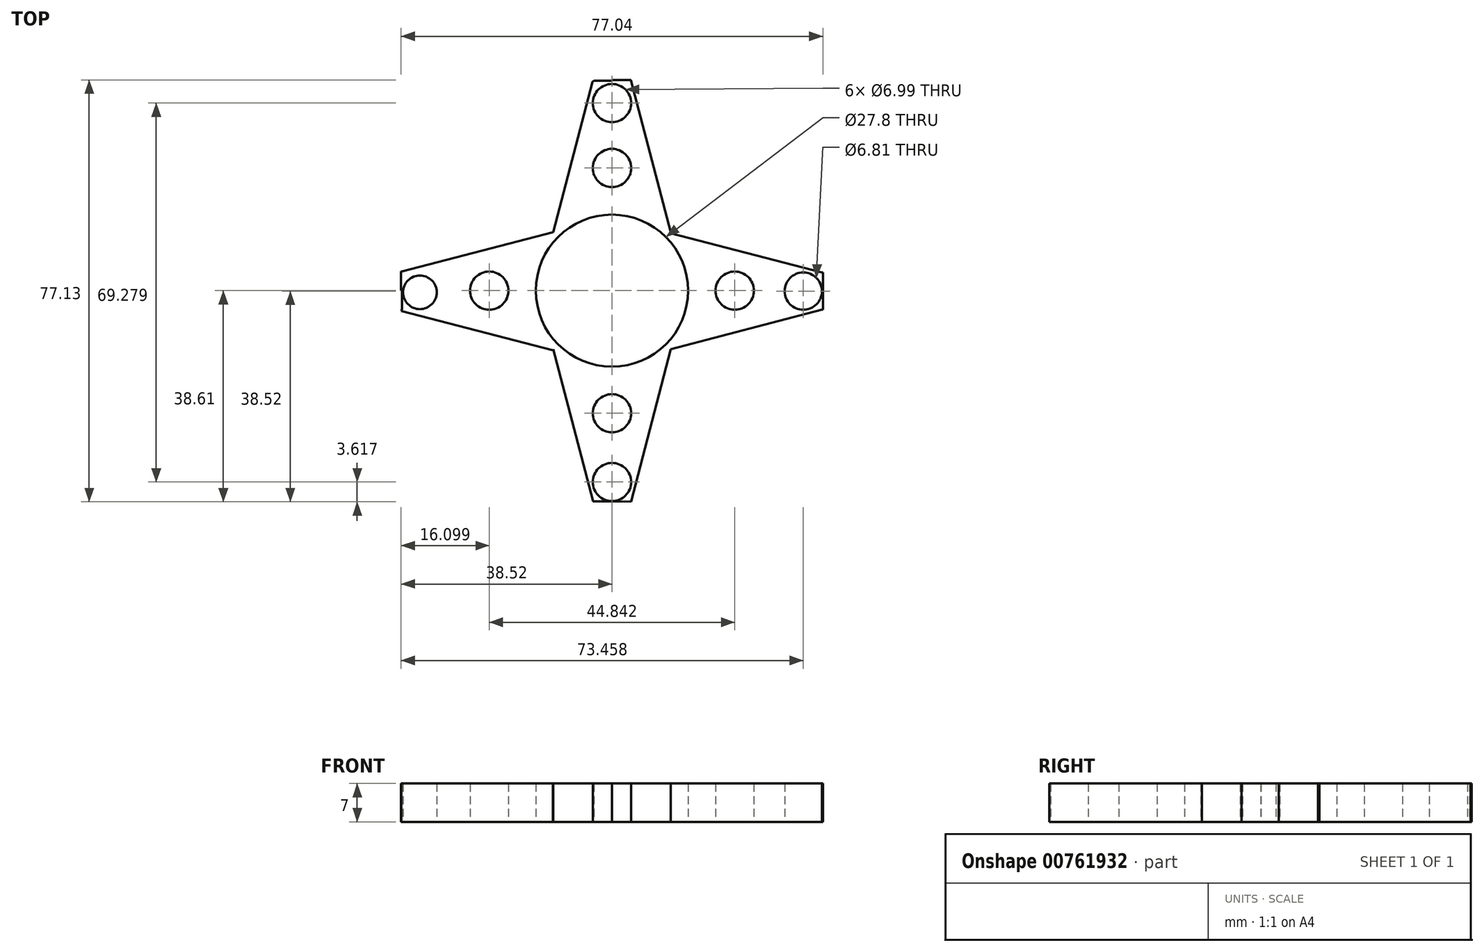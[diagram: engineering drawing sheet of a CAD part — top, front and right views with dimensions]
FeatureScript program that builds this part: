
annotation { "Feature Type Name" : "Feature", "Feature Type Description" : "" }
export const myFeature = defineFeature(function(context is Context, id is Id, definition is map)
    precondition{}
    {
        {
            var Q0;
            Q0=qCreatedBy(makeId("Top.planeOp"),FACE);
            var sketch = newSketch(context, id + "F0", { "sketchPlane" : qUnion([Q0])});
            skCircle(sketch, "E0", {"center": v(0, 0) * mm, "radius": 13.9 * mm});
            skPoint(sketch, "E1.start.orphan", {"position": v(7.44, 39.96) * mm});
            skPoint(sketch, "E2.start.orphan", {"position": v(0, 26.64) * mm});
            skPoint(sketch, "E3.orphan", {"position": v(0, 13.32) * mm});
            skPoint(sketch, "E4.MirrorCS.end.orphan", {"position": v(0, 39.96) * mm});
            skPoint(sketch, "E5.orphan", {"position": v(8.68, 13.32) * mm});
            skPoint(sketch, "E6.MirrorCS.end.orphan", {"position": v(-8.75, 13.32) * mm});
            skPoint(sketch, "E7.orphan", {"position": v(0, 30.02) * mm});
            skPoint(sketch, "E8.MirrorCS.start.orphan", {"position": v(0, 38.56) * mm});
            skCircle(sketch, "E9", {"center": v(0, 34.29) * mm, "radius": 3.5 * mm});
            skCircle(sketch, "E10.1.1", {"center": v(-35.09, -0.3) * mm, "radius": 3.08 * mm});
            skCircle(sketch, "E10.2.1", {"center": v(0, -35) * mm, "radius": 3.5 * mm});
            skCircle(sketch, "E10.3.1", {"center": v(34.94, -0.09) * mm, "radius": 3.4 * mm});
            skPoint(sketch, "E11.orphan", {"position": v(0, -13.9) * mm});
            skPoint(sketch, "E12.orphan", {"position": v(13.32, 0) * mm});
            skPoint(sketch, "E13.orphan", {"position": v(0, -13.32) * mm});
            skPoint(sketch, "E14.start.orphan", {"position": v(0, 13.9) * mm});
            skCircle(sketch, "E15.MirrorC", {"center": v(-22.42, 0) * mm, "radius": 3.5 * mm});
            skCircle(sketch, "E16.1.0", {"center": v(0, -22.42) * mm, "radius": 3.5 * mm});
            skCircle(sketch, "E16.2.0", {"center": v(22.42, 0) * mm, "radius": 3.5 * mm});
            skCircle(sketch, "E16.3.0", {"center": v(0, 22.42) * mm, "radius": 3.5 * mm});
            skPoint(sketch, "E17.orphan", {"position": v(-29.02, 12.82) * mm});
            skPoint(sketch, "E18.orphan", {"position": v(-13.9, 0) * mm});
            skPoint(sketch, "E19.orphan", {"position": v(-29.02, -0.23) * mm});
            skPoint(sketch, "E20.start.orphan", {"position": v(-22.96, -0.15) * mm});
            skPoint(sketch, "E21.start.orphan", {"position": v(-32.01, -0.3) * mm});
            skPoint(sketch, "E22.start.orphan", {"position": v(34.94, -3.5) * mm});
            skPoint(sketch, "E23.start.orphan", {"position": v(38.33, -3.5) * mm});
            skPoint(sketch, "E24.start.orphan", {"position": v(34.94, 3.32) * mm});
            skLineSegment(sketch, "E25.MirrorCS", {"start": v(38.52, 0) * mm, "end": v(38.52, -3.5) * mm});
            skLineSegment(sketch, "E26", {"start": v(38.35, 3.32) * mm, "end": v(10.66, 10.5) * mm});
            skLineSegment(sketch, "E27", {"start": v(38.33, -3.5) * mm, "end": v(10.71, -10.71) * mm});
            skPoint(sketch, "E28.start.orphan", {"position": v(3.5, 34.29) * mm});
            skPoint(sketch, "E29.start.orphan", {"position": v(-3.5, 34.29) * mm});
            skPoint(sketch, "E30.start.orphan", {"position": v(-35.09, 2.77) * mm});
            skPoint(sketch, "E31.start.orphan", {"position": v(-35.09, -3.38) * mm});
            skPoint(sketch, "E32.start.orphan", {"position": v(3.5, -35) * mm});
            skPoint(sketch, "E33.start.orphan", {"position": v(-3.5, -35) * mm});
            skPoint(sketch, "E34.orphan", {"position": v(-16.14, 34.94) * mm});
            skPoint(sketch, "E35.orphan", {"position": v(3.77, -14.48) * mm});
            skLineSegment(sketch, "E36.1.0", {"start": v(0.09, 38.35) * mm, "end": v(-3.32, 38.35) * mm});
            skLineSegment(sketch, "E36.1.1", {"start": v(3.5, 38.33) * mm, "end": v(10.71, 10.71) * mm});
            skLineSegment(sketch, "E36.1.2", {"start": v(0, 38.52) * mm, "end": v(3.5, 38.52) * mm});
            skLineSegment(sketch, "E36.2.0", {"start": v(-38.35, 0.09) * mm, "end": v(-38.35, -3.32) * mm});
            skLineSegment(sketch, "E36.2.1", {"start": v(-38.33, 3.5) * mm, "end": v(-10.71, 10.71) * mm});
            skLineSegment(sketch, "E36.2.2", {"start": v(-38.52, 0) * mm, "end": v(-38.52, 3.5) * mm});
            skLineSegment(sketch, "E36.3.0", {"start": v(-0.09, -38.35) * mm, "end": v(3.32, -38.35) * mm});
            skLineSegment(sketch, "E36.3.1", {"start": v(-3.5, -38.33) * mm, "end": v(-10.71, -10.71) * mm});
            skLineSegment(sketch, "E36.3.2", {"start": v(0, -38.52) * mm, "end": v(-3.5, -38.52) * mm});
            skLineSegment(sketch, "E37.1.0", {"start": v(-3.58, 38.2) * mm, "end": v(-10.77, 10.5) * mm});
            skLineSegment(sketch, "E37.2.0", {"start": v(-38.45, -3.74) * mm, "end": v(-10.77, -10.92) * mm});
            skLineSegment(sketch, "E37.3.0", {"start": v(3.47, -38.6) * mm, "end": v(10.66, -10.92) * mm});
            skPoint(sketch, "E37.center", {"position": v(-0.05, -0.2) * mm});
            skPoint(sketch, "E38.orphan", {"position": v(3.92, 14.64) * mm});
            skLineSegment(sketch, "E39", {"start": v(3.5, 38.52) * mm, "end": v(3.5, 38.33) * mm});
            skLineSegment(sketch, "E40", {"start": v(38.52, -3.5) * mm, "end": v(38.33, -3.5) * mm});
            skLineSegment(sketch, "E41", {"start": v(-3.5, -38.52) * mm, "end": v(-3.5, -38.33) * mm});
            skLineSegment(sketch, "E42", {"start": v(-38.52, 3.5) * mm, "end": v(-38.33, 3.5) * mm});
            skLineSegment(sketch, "E43", {"start": v(38.52, -3.5) * mm, "end": v(38.52, 3.32) * mm});
            skLineSegment(sketch, "E44", {"start": v(38.52, 3.32) * mm, "end": v(38.35, 3.32) * mm});
            skPoint(sketch, "E45.start.orphan", {"position": v(38.35, -0.09) * mm});
            skLineSegment(sketch, "E46", {"start": v(10.71, 10.71) * mm, "end": v(10.66, 10.5) * mm});
            skLineSegment(sketch, "E47", {"start": v(10.71, -10.71) * mm, "end": v(10.66, -10.92) * mm});
            skLineSegment(sketch, "E48", {"start": v(-10.71, -10.71) * mm, "end": v(-10.77, -10.92) * mm});
            skLineSegment(sketch, "E49", {"start": v(3.32, -38.35) * mm, "end": v(3.47, -38.6) * mm});
            skLineSegment(sketch, "E50", {"start": v(0.09, 38.35) * mm, "end": v(0, 38.52) * mm});
            skLineSegment(sketch, "E51", {"start": v(-3.32, 38.35) * mm, "end": v(-3.58, 38.2) * mm});
            skLineSegment(sketch, "E52", {"start": v(-38.45, -3.74) * mm, "end": v(-38.35, -3.32) * mm});
            skLineSegment(sketch, "E53", {"start": v(0, -38.52) * mm, "end": v(3.47, -38.6) * mm});
            skLineSegment(sketch, "E54", {"start": v(-38.35, 0.09) * mm, "end": v(-38.52, 0) * mm});
            skSolve(sketch);
        }
        {
            var Q0;
            Q0 = qSketchRegion(id + "F0", true);
            extrude(context, id + "F1", {"entities" : qUnion([Q0]), "depth" : 7 * mm, "offsetDistance" : 25 * mm});
        }
    });
